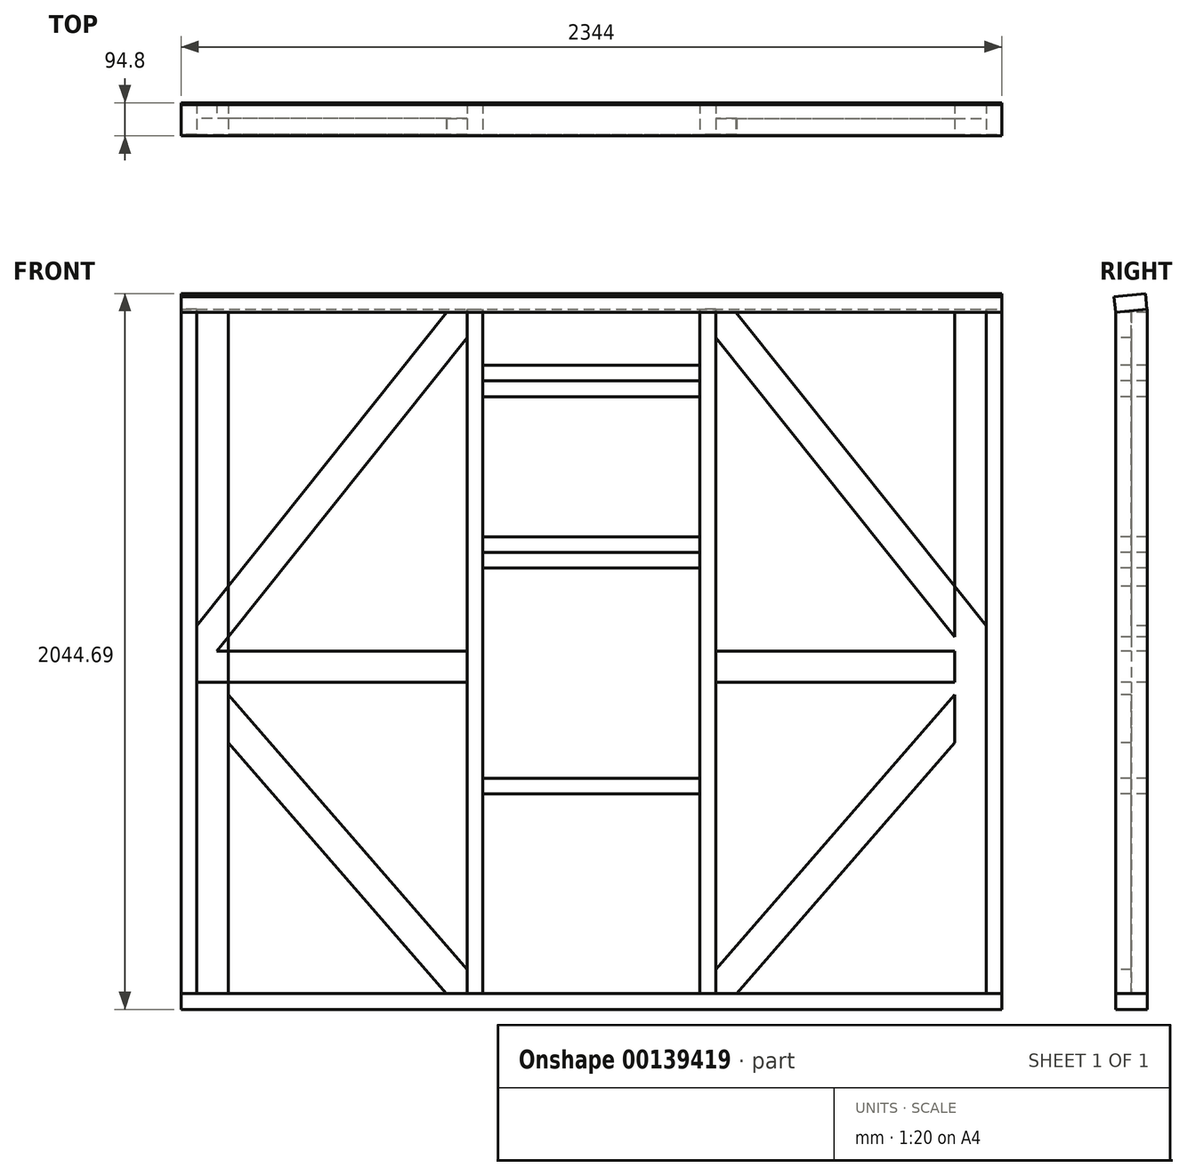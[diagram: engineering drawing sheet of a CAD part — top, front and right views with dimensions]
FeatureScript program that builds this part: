
annotation { "Feature Type Name" : "Feature", "Feature Type Description" : "" }
export const myFeature = defineFeature(function(context is Context, id is Id, definition is map)
    precondition{}
    {
        {
            var Q0;
            Q0=qCreatedBy(makeId("Top.planeOp"),FACE);
            var sketch = newSketch(context, id + "F0", { "sketchPlane" : qUnion([Q0])});
            skLineSegment(sketch, "E0.bottom", {"start": v(-1172, 45) * mm, "end": v(1172, 45) * mm});
            skLineSegment(sketch, "E0.top", {"start": v(-1172, -45) * mm, "end": v(1172, -45) * mm});
            skLineSegment(sketch, "E0.left", {"start": v(-1172, 45) * mm, "end": v(-1172, -45) * mm});
            skLineSegment(sketch, "E0.right", {"start": v(1172, 45) * mm, "end": v(1172, -45) * mm});
            skSolve(sketch);
        }
        {
            var Q0;
            Q0=makeQuery(id+"F0.imprint","IMPRINT",FACE,{"disambiguationData":[TD([[makeQuery(id+"F0.imprint","IMPRINT",EDGE,{"derivedFrom":sQuery(id+"F0.wireOp",EDGE,"E0.bottom")}),-1.0]])]});
            extrude(context, id + "F1", {"entities" : qUnion([Q0]), "depth" : 45 * mm});
        }
        {
            var Q0;
            Q0=makeQuery(id+"F1.opExtrude","SWEPT_FACE",FACE,{"disambiguationData":[OSD([sQuery(id+"F0.wireOp",EDGE,"E0.left")])]});
            var sketch = newSketch(context, id + "F2", { "sketchPlane" : qUnion([Q0])});
            skPoint(sketch, "E1.oppositeSnap0", {"position": v(45, 22.5) * mm});
            skLineSegment(sketch, "E1.bottom", {"start": v(-45, 45) * mm, "end": v(45, 45) * mm});
            skLineSegment(sketch, "E1.top", {"start": v(-45, 1990.34) * mm, "end": v(45, 1990.34) * mm});
            skLineSegment(sketch, "E1.left", {"start": v(-45, 45) * mm, "end": v(-45, 1990.34) * mm});
            skLineSegment(sketch, "E1.right", {"start": v(45, 45) * mm, "end": v(45, 1990.34) * mm});
            skLineSegment(sketch, "E2", {"start": v(-45, 1990.34) * mm, "end": v(-45, 2000) * mm});
            skLineSegment(sketch, "E3", {"start": v(-45, 2000) * mm, "end": v(45, 1990.34) * mm});
            skSolve(sketch);
        }
        {
            var Q0;
            Q0=qCreatedBy(makeId("Right.planeOp"),FACE);
            cPlane(context, id + "F3", {"entities" : qUnion([Q0]), "cplaneType" : CPlaneType.OFFSET, "offset" : 310 * mm, "oppositeDirection" : true, "width" : 150 * mm, "height" : 150 * mm});
        }
        {
            var Q0;
            Q0=qCreatedBy(id+"F3.planeOp",FACE);
            var sketch = newSketch(context, id + "F4", { "sketchPlane" : qUnion([Q0])});
            skLineSegment(sketch, "E4.bottom", {"start": v(45, 0) * mm, "end": v(-45, 0) * mm});
            skLineSegment(sketch, "E4.top", {"start": v(45, 1990.34) * mm, "end": v(-45, 1990.34) * mm});
            skLineSegment(sketch, "E4.left", {"start": v(45, 0) * mm, "end": v(45, 1990.34) * mm});
            skLineSegment(sketch, "E4.right", {"start": v(-45, 0) * mm, "end": v(-45, 1990.34) * mm});
            skLineSegment(sketch, "E5", {"start": v(45, 1990.34) * mm, "end": v(45, 2000) * mm});
            skLineSegment(sketch, "E6", {"start": v(45, 2000) * mm, "end": v(-45, 1990.34) * mm});
            skLineSegment(sketch, "E7", {"start": v(45, 45) * mm, "end": v(-45, 45) * mm});
            skSolve(sketch);
        }
        {
            var Q0;
            Q0=makeQuery(id+"F2.imprint","IMPRINT",FACE,{"disambiguationData":[TD([[makeQuery(id+"F2.imprint","IMPRINT",EDGE,{"derivedFrom":sQuery(id+"F2.wireOp",EDGE,"E1.bottom")}),1.0]])]});
            var Q1;
            Q1=makeQuery(id+"F2.imprint","IMPRINT",FACE,{"disambiguationData":[TD([[makeQuery(id+"F2.imprint","IMPRINT",EDGE,{"derivedFrom":sQuery(id+"F2.wireOp",EDGE,"E1.top")}),1.0]])]});
            extrude(context, id + "F5", {"entities" : qUnion([Q0, Q1]), "oppositeDirection" : true, "depth" : 45 * mm});
        }
        {
            var Q0;
            Q0=makeQuery(id+"F5.opExtrude","SWEPT_BODY",BODY,{"disambiguationData":[OSD([sQuery(id+"F2.wireOp",EDGE,"E1.bottom"),sQuery(id+"F2.wireOp",EDGE,"E1.left"),sQuery(id+"F2.wireOp",EDGE,"E1.right"),sQuery(id+"F2.wireOp",EDGE,"E2"),sQuery(id+"F2.wireOp",EDGE,"E3")])]});
            var Q1;
            Q1=qCreatedBy(makeId("Right.planeOp"),FACE);
            mirror(context, id + "F6", {"entities" : qUnion([Q0]), "mirrorPlane" : qUnion([Q1])});
        }
        {
            var Q0;
            Q0=makeQuery(id+"F4.imprint","IMPRINT",FACE,{"disambiguationData":[TD([[makeQuery(id+"F4.imprint","IMPRINT",EDGE,{"derivedFrom":sQuery(id+"F4.wireOp",EDGE,"E4.top")}),-1.0]])]});
            var Q1;
            {var subQ0=sQuery(id+"F4.wireOp",EDGE,"E4.top");Q1=makeQuery(id+"F4.imprint","IMPRINT",FACE,{"disambiguationData":[TD([[makeQuery(id+"F4.imprint","IMPRINT",EDGE,{"derivedFrom":subQ0}),1.0]])]});}
            extrude(context, id + "F7", {"entities" : qUnion([Q0, Q1]), "oppositeDirection" : true, "depth" : 45 * mm});
        }
        {
            var Q0;
            Q0=makeQuery(id+"F5.opExtrude","SWEPT_FACE",FACE,{"disambiguationData":[OSD([sQuery(id+"F2.wireOp",EDGE,"E3")])]});
            var sketch = newSketch(context, id + "F8", { "sketchPlane" : qUnion([Q0])});
            skLineSegment(sketch, "E8.bottom", {"start": v(-1172, 167.6) * mm, "end": v(1172, 167.6) * mm});
            skLineSegment(sketch, "E8.top", {"start": v(-1172, 257.6) * mm, "end": v(1172, 257.6) * mm});
            skLineSegment(sketch, "E8.left", {"start": v(-1172, 167.6) * mm, "end": v(-1172, 257.6) * mm});
            skLineSegment(sketch, "E8.right", {"start": v(1172, 167.6) * mm, "end": v(1172, 257.6) * mm});
            skSolve(sketch);
        }
        {
            var Q0;
            {var subQ0=sQuery(id+"F8.wireOp",EDGE,"E8.left");Q0=makeQuery(id+"F8.imprint","IMPRINT",FACE,{"disambiguationData":[TD([[makeQuery(id+"F8.imprint","IMPRINT",EDGE,{"derivedFrom":subQ0}),1.0]])]});}
            var Q1;
            {var subQ3=sQuery(id+"F8.wireOp",EDGE,"E8.right");Q1=makeQuery(id+"F8.imprint","IMPRINT",FACE,{"disambiguationData":[TD([[makeQuery(id+"F8.imprint","IMPRINT",EDGE,{"derivedFrom":subQ3}),1.0]])]});}
            extrude(context, id + "F9", {"entities" : qUnion([Q0, Q1]), "depth" : 45 * mm});
        }
        {
            var Q0;
            Q0=makeQuery(id+"F7.opExtrude","SWEPT_FACE",FACE,{"disambiguationData":[OSD([sQuery(id+"F4.wireOp",EDGE,"E4.right")])]});
            var sketch = newSketch(context, id + "F10", { "sketchPlane" : qUnion([Q0])});
            skLineSegment(sketch, "E9.top", {"start": v(-310, 1795) * mm, "end": v(310, 1795) * mm});
            skLineSegment(sketch, "E9.right", {"start": v(310, 1750) * mm, "end": v(310, 1795) * mm});
            skLineSegment(sketch, "E10.top", {"start": v(-310, 1350) * mm, "end": v(310, 1350) * mm});
            skLineSegment(sketch, "E10.right", {"start": v(310, 1305) * mm, "end": v(310, 1350) * mm});
            skLineSegment(sketch, "E11.bottom", {"start": v(310, 1305) * mm, "end": v(-310, 1305) * mm});
            skLineSegment(sketch, "E11.left", {"start": v(310, 1305) * mm, "end": v(310, 1260) * mm});
            skLineSegment(sketch, "E12.left", {"start": v(310, 1795) * mm, "end": v(310, 1840) * mm});
            skLineSegment(sketch, "E13.bottom", {"start": v(-310, 660) * mm, "end": v(310, 660) * mm});
            skLineSegment(sketch, "E13.top", {"start": v(-310, 615) * mm, "end": v(310, 615) * mm});
            skLineSegment(sketch, "E13.right", {"start": v(310, 660) * mm, "end": v(310, 615) * mm});
            skLineSegment(sketch, "E14", {"start": v(0, 0) * mm, "end": v(0, 2847.43) * mm, "construction": true});
            skLineSegment(sketch, "E15", {"start": v(-1127, 45) * mm, "end": v(-1127, 1990.34) * mm});
            skLineSegment(sketch, "E16", {"start": v(-1127, 1990.34) * mm, "end": v(-1037, 1990.34) * mm});
            skLineSegment(sketch, "E17", {"start": v(-1037, 1990.34) * mm, "end": v(-1037, 45) * mm});
            skLineSegment(sketch, "E18", {"start": v(-1037, 45) * mm, "end": v(-1127, 45) * mm});
            skLineSegment(sketch, "E19", {"start": v(-355, 933.74) * mm, "end": v(-355, 1023.74) * mm});
            skLineSegment(sketch, "E20", {"start": v(-355, 1990.34) * mm, "end": v(-412.6, 1990.34) * mm});
            skLineSegment(sketch, "E21", {"start": v(-355, 1990.34) * mm, "end": v(-355, 1918.24) * mm});
            skLineSegment(sketch, "E22", {"start": v(-414.6, 45) * mm, "end": v(-355, 45) * mm});
            skLineSegment(sketch, "E23", {"start": v(-355, 45) * mm, "end": v(-355, 113.62) * mm});
            skLineSegment(sketch, "E24", {"start": v(-310, 1840) * mm, "end": v(-310, 1795) * mm});
            skLineSegment(sketch, "E25", {"start": v(310, 1840) * mm, "end": v(-310, 1840) * mm});
            skLineSegment(sketch, "E26", {"start": v(310, 1750) * mm, "end": v(-310, 1750) * mm});
            skLineSegment(sketch, "E27", {"start": v(-310, 1750) * mm, "end": v(-310, 1795) * mm});
            skLineSegment(sketch, "E28", {"start": v(310, 1260) * mm, "end": v(-310, 1260) * mm});
            skLineSegment(sketch, "E29", {"start": v(-310, 1260) * mm, "end": v(-310, 1305) * mm});
            skLineSegment(sketch, "E30", {"start": v(-310, 1350) * mm, "end": v(-310, 1305) * mm});
            skLineSegment(sketch, "E31", {"start": v(-310, 660) * mm, "end": v(-310, 615) * mm});
            skLineSegment(sketch, "E32", {"start": v(-355, 1990.34) * mm, "end": v(-1127, 1023.74) * mm, "construction": true});
            skLineSegment(sketch, "E33", {"start": v(-412.6, 1990.34) * mm, "end": v(-1127, 1095.85) * mm});
            skLineSegment(sketch, "E34", {"start": v(-1127, 1095.85) * mm, "end": v(-1127, 1023.74) * mm});
            skLineSegment(sketch, "E35", {"start": v(-355, 1918.24) * mm, "end": v(-1069.4, 1023.74) * mm});
            skLineSegment(sketch, "E36", {"start": v(-1127, 933.74) * mm, "end": v(-1127, 1023.74) * mm});
            skLineSegment(sketch, "E37", {"start": v(-1127, 933.74) * mm, "end": v(-355, 45) * mm, "construction": true});
            skLineSegment(sketch, "E38", {"start": v(-355, 113.62) * mm, "end": v(-1067.4, 933.74) * mm});
            skLineSegment(sketch, "E39", {"start": v(-1067.4, 933.74) * mm, "end": v(-1127, 933.74) * mm});
            skLineSegment(sketch, "E40", {"start": v(-414.6, 45) * mm, "end": v(-1127, 865.12) * mm});
            skLineSegment(sketch, "E41", {"start": v(-1127, 865.12) * mm, "end": v(-1127, 933.74) * mm});
            skLineSegment(sketch, "E42", {"start": v(-1127, 978.74) * mm, "end": v(-355, 978.74) * mm, "construction": true});
            skLineSegment(sketch, "E43", {"start": v(-355, 1023.74) * mm, "end": v(-1127, 1023.74) * mm});
            skLineSegment(sketch, "E44", {"start": v(-1067.4, 933.74) * mm, "end": v(-355, 933.74) * mm});
            skSolve(sketch);
        }
        {
            var Q0;
            Q0=makeQuery(id+"F10.imprint","IMPRINT",FACE,{"disambiguationData":[TD([[makeQuery(id+"F10.imprint","IMPRINT",EDGE,{"derivedFrom":sQuery(id+"F10.wireOp",EDGE,"aNH3sxCa-MStV-n3YT-x1Xh-w2WQ0LI5mPOo.bottom")}),1.0]])]});
            var Q1;
            Q1=makeQuery(id+"F10.imprint","IMPRINT",FACE,{"disambiguationData":[TD([[makeQuery(id+"F10.imprint","IMPRINT",EDGE,{"derivedFrom":sQuery(id+"F10.wireOp",EDGE,"E11.bottom")}),1.0]])]});
            var Q2;
            Q2=makeQuery(id+"F10.imprint","IMPRINT",FACE,{"disambiguationData":[TD([[makeQuery(id+"F10.imprint","IMPRINT",EDGE,{"derivedFrom":sQuery(id+"F10.wireOp",EDGE,"Ij1T8FEQ-5BbB-TQYr-fU45-vdiwiW7gqSCe.bottom")}),1.0]])]});
            var Q3;
            Q3=makeQuery(id+"F10.imprint","IMPRINT",FACE,{"disambiguationData":[TD([[makeQuery(id+"F10.imprint","IMPRINT",EDGE,{"derivedFrom":sQuery(id+"F10.wireOp",EDGE,"E9.bottom")}),1.0]])]});
            var Q4;
            {var subQ0=sQuery(id+"F10.wireOp",EDGE,"eWYLrNJm-et1t-QfGm-Zsnl-IqfbEICfQMLq");Q4=makeQuery(id+"F10.imprint","IMPRINT",FACE,{"disambiguationData":[TD([[makeQuery(id+"F10.imprint","IMPRINT",EDGE,{"derivedFrom":subQ0}),1.0]])]});}
            var Q5;
            Q5=makeQuery(id+"F10.imprint","IMPRINT",FACE,{"disambiguationData":[TD([[makeQuery(id+"F10.imprint","IMPRINT",EDGE,{"derivedFrom":sQuery(id+"F10.wireOp",EDGE,"h7dogYSd-q6sY-grKT-snfd-gdXiXc72r8yc")}),-1.0]])]});
            var Q6;
            Q6=makeQuery(id+"F10.imprint","IMPRINT",FACE,{"disambiguationData":[TD([[makeQuery(id+"F10.imprint","IMPRINT",EDGE,{"derivedFrom":sQuery(id+"F10.wireOp",EDGE,"LHV4K2mJ-eiuq-82WD-fQUk-1G5o7ke3O5lb")}),1.0]])]});
            var Q7;
            Q7=makeQuery(id+"F10.imprint","IMPRINT",FACE,{"disambiguationData":[TD([[makeQuery(id+"F10.imprint","IMPRINT",EDGE,{"derivedFrom":sQuery(id+"F10.wireOp",EDGE,"E9.top")}),-1.0]])]});
            extrude(context, id + "F11", {"entities" : qUnion([Q0, Q1, Q2, Q3, Q4, Q5, Q6, Q7]), "oppositeDirection" : true, "depth" : 90 * mm});
        }
        {
            var Q0;
            Q0=makeQuery(id+"F10.imprint","IMPRINT",FACE,{"disambiguationData":[TD([[makeQuery(id+"F10.imprint","IMPRINT",EDGE,{"derivedFrom":sQuery(id+"F10.wireOp",EDGE,"vieiSLFH-R6ZJ-pJ7R-J9bz-VHSQ9F03vbUm")}),-1.0]])]});
            var Q1;
            {var subQ1=sQuery(id+"F10.wireOp",EDGE,"wrMeRyHu-uC7o-dnzY-bJ9c-UQa0hcCIsVim");Q1=makeQuery(id+"F10.imprint","IMPRINT",FACE,{"disambiguationData":[TD([[makeQuery(id+"F10.imprint","IMPRINT",EDGE,{"derivedFrom":subQ1}),1.0]])]});}
            var Q2;
            Q2=makeQuery(id+"F10.imprint","IMPRINT",FACE,{"disambiguationData":[TD([[makeQuery(id+"F10.imprint","IMPRINT",EDGE,{"derivedFrom":sQuery(id+"F10.wireOp",EDGE,"E13.bottom")}),-1.0]])]});
            var Q3;
            Q3=makeQuery(id+"F10.imprint","IMPRINT",FACE,{"disambiguationData":[TD([[makeQuery(id+"F10.imprint","IMPRINT",EDGE,{"derivedFrom":sQuery(id+"F10.wireOp",EDGE,"E10.top")}),-1.0]])]});
            var Q4;
            Q4=makeQuery(id+"F10.imprint","IMPRINT",FACE,{"disambiguationData":[TD([[makeQuery(id+"F10.imprint","IMPRINT",EDGE,{"derivedFrom":sQuery(id+"F10.wireOp",EDGE,"E12.bottom")}),-1.0]])]});
            var Q5;
            Q5=makeQuery(id+"F10.imprint","IMPRINT",FACE,{"disambiguationData":[TD([[makeQuery(id+"F10.imprint","IMPRINT",EDGE,{"derivedFrom":sQuery(id+"F10.wireOp",EDGE,"Lcdz85kG-cBBN-Ayva-E4xm-H0MH0zZ8DXnZ")}),1.0]])]});
            var Q6;
            {var subQ0=sQuery(id+"F10.wireOp",EDGE,"0AAHXuRS-wDEC-8Cf9-syur-U7LPKP8lYQoM.bottom");Q6=makeQuery(id+"F10.imprint","IMPRINT",FACE,{"disambiguationData":[TD([[makeQuery(id+"F10.imprint","IMPRINT",EDGE,{"derivedFrom":subQ0}),1.0]])]});}
            var Q7;
            Q7=makeQuery(id+"F10.imprint","IMPRINT",FACE,{"disambiguationData":[TD([[makeQuery(id+"F10.imprint","IMPRINT",EDGE,{"derivedFrom":sQuery(id+"F10.wireOp",EDGE,"E9.top")}),1.0]])]});
            extrude(context, id + "F12", {"entities" : qUnion([Q0, Q1, Q2, Q3, Q4, Q5, Q6, Q7]), "oppositeDirection" : true, "depth" : 90 * mm});
        }
        {
            var Q0;
            {var subQ5=sQuery(id+"F10.wireOp",EDGE,"IWMOSWK4-ciEs-Mal6-oFdt-2DP9KBoqK9iO");Q0=makeQuery(id+"F10.imprint","IMPRINT",FACE,{"disambiguationData":[TD([[makeQuery(id+"F10.imprint","IMPRINT",EDGE,{"derivedFrom":subQ5}),1.0]])]});}
            var Q1;
            {var subQ5=sQuery(id+"F10.wireOp",EDGE,"ps9piARj-ZZIE-nllt-Hb1m-invj6BAIlQQJ");Q1=makeQuery(id+"F10.imprint","IMPRINT",FACE,{"disambiguationData":[TD([[makeQuery(id+"F10.imprint","IMPRINT",EDGE,{"derivedFrom":subQ5}),1.0]])]});}
            var Q2;
            {var subQ5=sQuery(id+"F10.wireOp",EDGE,"yZNBr7LE-ELaA-HA4S-0qR6-vm5n6uQIesuE");Q2=makeQuery(id+"F10.imprint","IMPRINT",FACE,{"disambiguationData":[TD([[makeQuery(id+"F10.imprint","IMPRINT",EDGE,{"derivedFrom":subQ5}),-1.0]])]});}
            var Q3;
            {var subQ5=sQuery(id+"F10.wireOp",EDGE,"dmxOI3Du-O8Xy-rVEy-b6zb-gbipeINEvBco");Q3=makeQuery(id+"F10.imprint","IMPRINT",FACE,{"disambiguationData":[TD([[makeQuery(id+"F10.imprint","IMPRINT",EDGE,{"derivedFrom":subQ5}),-1.0]])]});}
            var Q4;
            {var subQ6=sQuery(id+"F10.wireOp",EDGE,"E20");Q4=makeQuery(id+"F10.imprint","IMPRINT",FACE,{"disambiguationData":[TD([[makeQuery(id+"F10.imprint","IMPRINT",EDGE,{"derivedFrom":subQ6}),1.0]])]});}
            var Q5;
            {var subQ0=sQuery(id+"F10.wireOp",EDGE,"KczKcjUI-WOQ1-k2C4-5KFe-5vsth0F9XvNb");Q5=makeQuery(id+"F10.imprint","IMPRINT",FACE,{"disambiguationData":[TD([[makeQuery(id+"F10.imprint","IMPRINT",EDGE,{"derivedFrom":subQ0}),1.0]])]});}
            var Q6;
            {var subQ0=sQuery(id+"F10.wireOp",EDGE,"E22");Q6=makeQuery(id+"F10.imprint","IMPRINT",FACE,{"disambiguationData":[TD([[makeQuery(id+"F10.imprint","IMPRINT",EDGE,{"derivedFrom":subQ0}),1.0]])]});}
            var Q7;
            {var subQ0=sQuery(id+"F10.wireOp",EDGE,"TkALrY8s-t1C9-4eny-qfDH-DOJZUvdrRhiO");Q7=makeQuery(id+"F10.imprint","IMPRINT",FACE,{"disambiguationData":[TD([[makeQuery(id+"F10.imprint","IMPRINT",EDGE,{"derivedFrom":subQ0}),1.0]])]});}
            var Q8;
            {var subQ5=sQuery(id+"F10.wireOp",EDGE,"E34");Q8=makeQuery(id+"F10.imprint","IMPRINT",FACE,{"disambiguationData":[TD([[makeQuery(id+"F10.imprint","IMPRINT",EDGE,{"derivedFrom":subQ5}),1.0]])]});}
            var Q9;
            {var subQ5=sQuery(id+"F10.wireOp",EDGE,"E41");Q9=makeQuery(id+"F10.imprint","IMPRINT",FACE,{"disambiguationData":[TD([[makeQuery(id+"F10.imprint","IMPRINT",EDGE,{"derivedFrom":subQ5}),-1.0]])]});}
            extrude(context, id + "F13", {"entities" : qUnion([Q0, Q1, Q2, Q3, Q4, Q5, Q6, Q7, Q8, Q9]), "oppositeDirection" : true, "depth" : 45 * mm});
        }
        {
            var Q0;
            {var subQ5=sQuery(id+"F10.wireOp",EDGE,"E36");Q0=makeQuery(id+"F10.imprint","IMPRINT",FACE,{"disambiguationData":[TD([[makeQuery(id+"F10.imprint","IMPRINT",EDGE,{"derivedFrom":subQ5}),-1.0]])]});}
            var Q1;
            {var subQ0=sQuery(id+"F10.wireOp",EDGE,"E19");Q1=makeQuery(id+"F10.imprint","IMPRINT",FACE,{"disambiguationData":[TD([[makeQuery(id+"F10.imprint","IMPRINT",EDGE,{"derivedFrom":subQ0}),1.0]])]});}
            extrude(context, id + "F14", {"entities" : qUnion([Q0, Q1]), "oppositeDirection" : true, "depth" : 45 * mm});
        }
        {
            var Q0;
            Q0=makeQuery(id+"F13.opExtrude","SWEPT_BODY",BODY,{"disambiguationData":[OSD([sQuery(id+"F10.wireOp",EDGE,"yqz6w64T-0FIa-CpMf-ClYN-w0QtIlx0KdXD"),sQuery(id+"F10.wireOp",EDGE,"IWMOSWK4-ciEs-Mal6-oFdt-2DP9KBoqK9iO"),sQuery(id+"F10.wireOp",EDGE,"uspitZxR-TdZ1-jl7M-dguz-yieJGMehMW8g"),sQuery(id+"F10.wireOp",EDGE,"ps9piARj-ZZIE-nllt-Hb1m-invj6BAIlQQJ")])]});
            var Q1;
            Q1=makeQuery(id+"F13.opExtrude","SWEPT_BODY",BODY,{"disambiguationData":[OSD([sQuery(id+"F10.wireOp",EDGE,"WDCfjCSk-bBKj-UHSI-Wwkv-sx6gMcZcxZG9"),sQuery(id+"F10.wireOp",EDGE,"C1RgBI4g-g9TA-pd7b-vcFI-HoFZ3csmU8pP"),sQuery(id+"F10.wireOp",EDGE,"5TEl6OPY-4X05-3Ilv-CwpA-zPF8SHt4KhRh"),sQuery(id+"F10.wireOp",EDGE,"E19")])]});
            var Q2;
            Q2=makeQuery(id+"F13.opExtrude","SWEPT_BODY",BODY,{"disambiguationData":[OSD([sQuery(id+"F10.wireOp",EDGE,"y8FYGvt9-WakY-4leL-IbKU-3qXOnaKtpt7Q"),sQuery(id+"F10.wireOp",EDGE,"dmxOI3Du-O8Xy-rVEy-b6zb-gbipeINEvBco"),sQuery(id+"F10.wireOp",EDGE,"t5MrRVRE-BGiV-IxpZ-waTD-GKn7dtQTzOGG"),sQuery(id+"F10.wireOp",EDGE,"yZNBr7LE-ELaA-HA4S-0qR6-vm5n6uQIesuE")])]});
            var Q3;
            Q3=makeQuery(id+"FJZPI46I2R5lrBa_7.opExtrude","SWEPT_BODY",BODY,{"disambiguationData":[OSD([sQuery(id+"F10.wireOp",EDGE,"E15"),sQuery(id+"F10.wireOp",EDGE,"E16"),sQuery(id+"F10.wireOp",EDGE,"E17"),sQuery(id+"F10.wireOp",EDGE,"E18"),sQuery(id+"F10.wireOp",EDGE,"C1RgBI4g-g9TA-pd7b-vcFI-HoFZ3csmU8pP"),sQuery(id+"F10.wireOp",EDGE,"ps9piARj-ZZIE-nllt-Hb1m-invj6BAIlQQJ"),sQuery(id+"F10.wireOp",EDGE,"yZNBr7LE-ELaA-HA4S-0qR6-vm5n6uQIesuE")])]});
            var Q4;
            Q4=makeQuery(id+"F7.opExtrude","SWEPT_BODY",BODY,{"disambiguationData":[OSD([sQuery(id+"F4.wireOp",EDGE,"E4.left"),sQuery(id+"F4.wireOp",EDGE,"E4.right"),sQuery(id+"F4.wireOp",EDGE,"E5"),sQuery(id+"F4.wireOp",EDGE,"E6"),sQuery(id+"F4.wireOp",EDGE,"E7")])]});
            var Q5;
            Q5=makeQuery(id+"F13.opExtrude","SWEPT_BODY",BODY,{"disambiguationData":[OSD([sQuery(id+"F10.wireOp",EDGE,"sqicQ1Ev-1KLq-6kI6-2GGE-ZYKpb5yuFVKX"),sQuery(id+"F10.wireOp",EDGE,"nudTUXbH-r9Dm-7Fj1-w5Cs-egZg2BsbpaBh"),sQuery(id+"F10.wireOp",EDGE,"E20"),sQuery(id+"F10.wireOp",EDGE,"E21"),sQuery(id+"F10.wireOp",EDGE,"KczKcjUI-WOQ1-k2C4-5KFe-5vsth0F9XvNb"),sQuery(id+"F10.wireOp",EDGE,"y1xgUyTG-gkyS-6Niu-g9rG-T4ZHpyyhWdyM")])]});
            var Q6;
            Q6=makeQuery(id+"F14.opExtrude","SWEPT_BODY",BODY,{"disambiguationData":[OSD([sQuery(id+"F10.wireOp",EDGE,"WDCfjCSk-bBKj-UHSI-Wwkv-sx6gMcZcxZG9"),sQuery(id+"F10.wireOp",EDGE,"C1RgBI4g-g9TA-pd7b-vcFI-HoFZ3csmU8pP"),sQuery(id+"F10.wireOp",EDGE,"5TEl6OPY-4X05-3Ilv-CwpA-zPF8SHt4KhRh"),sQuery(id+"F10.wireOp",EDGE,"E19"),sQuery(id+"F10.wireOp",EDGE,"y1xgUyTG-gkyS-6Niu-g9rG-T4ZHpyyhWdyM"),sQuery(id+"F10.wireOp",EDGE,"TkALrY8s-t1C9-4eny-qfDH-DOJZUvdrRhiO")])]});
            var Q7;
            Q7=makeQuery(id+"F13.opExtrude","SWEPT_BODY",BODY,{"disambiguationData":[OSD([sQuery(id+"F10.wireOp",EDGE,"FKR76T0b-e7zS-v9PE-PyRv-utiDtJa5iY5K"),sQuery(id+"F10.wireOp",EDGE,"ZcPepuQs-37v6-5g6P-8xoM-8lzSBToUuJcQ"),sQuery(id+"F10.wireOp",EDGE,"TkALrY8s-t1C9-4eny-qfDH-DOJZUvdrRhiO"),sQuery(id+"F10.wireOp",EDGE,"nCsMJ4Dz-5rus-Vs0J-3G0T-E4C3YZWdDYXN"),sQuery(id+"F10.wireOp",EDGE,"E22"),sQuery(id+"F10.wireOp",EDGE,"E23")])]});
            var Q8;
            Q8=qCreatedBy(makeId("Right.planeOp"),FACE);
            mirror(context, id + "F15", {"entities" : qUnion([Q0, Q1, Q2, Q3, Q4, Q5, Q6, Q7]), "mirrorPlane" : qUnion([Q8])});
        }
        {
            var Q0;
            {var subQ0=sQuery(id+"F10.wireOp",EDGE,"E16");Q0=makeQuery(id+"F10.imprint","IMPRINT",FACE,{"disambiguationData":[TD([[makeQuery(id+"F10.imprint","IMPRINT",EDGE,{"derivedFrom":subQ0}),-1.0]])]});}
            var Q1;
            {var subQ5=sQuery(id+"F10.wireOp",EDGE,"E34");Q1=makeQuery(id+"F10.imprint","IMPRINT",FACE,{"disambiguationData":[TD([[makeQuery(id+"F10.imprint","IMPRINT",EDGE,{"derivedFrom":subQ5}),1.0]])]});}
            var Q2;
            {var subQ0=sQuery(id+"F10.wireOp",EDGE,"E35");var subQ1=sQuery(id+"F10.wireOp",EDGE,"E17");var subQ2=makeQuery(id+"F10.imprint","INTERSECT",VERTEX,{"derivedFrom":[subQ1,subQ0]});Q2=makeQuery(id+"F10.imprint","IMPRINT",FACE,{"disambiguationData":[TD([[makeQuery(id+"F10.imprint","IMPRINT",EDGE,{"disambiguationData":[TD([[subQ2,-1.0]])],"derivedFrom":subQ1}),-1.0]])]});}
            var Q3;
            {var subQ5=sQuery(id+"F10.wireOp",EDGE,"E36");Q3=makeQuery(id+"F10.imprint","IMPRINT",FACE,{"disambiguationData":[TD([[makeQuery(id+"F10.imprint","IMPRINT",EDGE,{"derivedFrom":subQ5}),-1.0]])]});}
            var Q4;
            {var subQ0=sQuery(id+"F10.wireOp",EDGE,"E44");var subQ1=sQuery(id+"F10.wireOp",EDGE,"E17");var subQ2=makeQuery(id+"F10.imprint","INTERSECT",VERTEX,{"derivedFrom":[subQ1,subQ0]});Q4=makeQuery(id+"F10.imprint","IMPRINT",FACE,{"disambiguationData":[TD([[makeQuery(id+"F10.imprint","IMPRINT",EDGE,{"disambiguationData":[TD([[subQ2,-1.0]])],"derivedFrom":subQ1}),-1.0]])]});}
            var Q5;
            {var subQ4=sQuery(id+"F10.wireOp",EDGE,"E39");Q5=makeQuery(id+"F10.imprint","IMPRINT",FACE,{"disambiguationData":[TD([[makeQuery(id+"F10.imprint","IMPRINT",EDGE,{"derivedFrom":subQ4}),1.0]])]});}
            var Q6;
            {var subQ0=sQuery(id+"F10.wireOp",EDGE,"E18");Q6=makeQuery(id+"F10.imprint","IMPRINT",FACE,{"disambiguationData":[TD([[makeQuery(id+"F10.imprint","IMPRINT",EDGE,{"derivedFrom":subQ0}),-1.0]])]});}
            extrude(context, id + "F16", {"entities" : qUnion([Q0, Q1, Q2, Q3, Q4, Q5, Q6]), "oppositeDirection" : true, "depth" : 90 * mm, "hasSecondDirection" : true, "secondDirectionOppositeDirection" : true, "secondDirectionDepth" : 45 * mm});
        }
        {
            var Q0;
            Q0=makeQuery(id+"F16.opExtrude","SWEPT_BODY",BODY,{"disambiguationData":[OSD([sQuery(id+"F10.wireOp",EDGE,"E15"),sQuery(id+"F10.wireOp",EDGE,"E16"),sQuery(id+"F10.wireOp",EDGE,"E17"),sQuery(id+"F10.wireOp",EDGE,"E18"),sQuery(id+"F10.wireOp",EDGE,"E34"),sQuery(id+"F10.wireOp",EDGE,"E36"),sQuery(id+"F10.wireOp",EDGE,"E41")])]});
            var Q1;
            Q1=qCreatedBy(makeId("Right.planeOp"),FACE);
            mirror(context, id + "F17", {"entities" : qUnion([Q0]), "mirrorPlane" : qUnion([Q1])});
        }
    });
